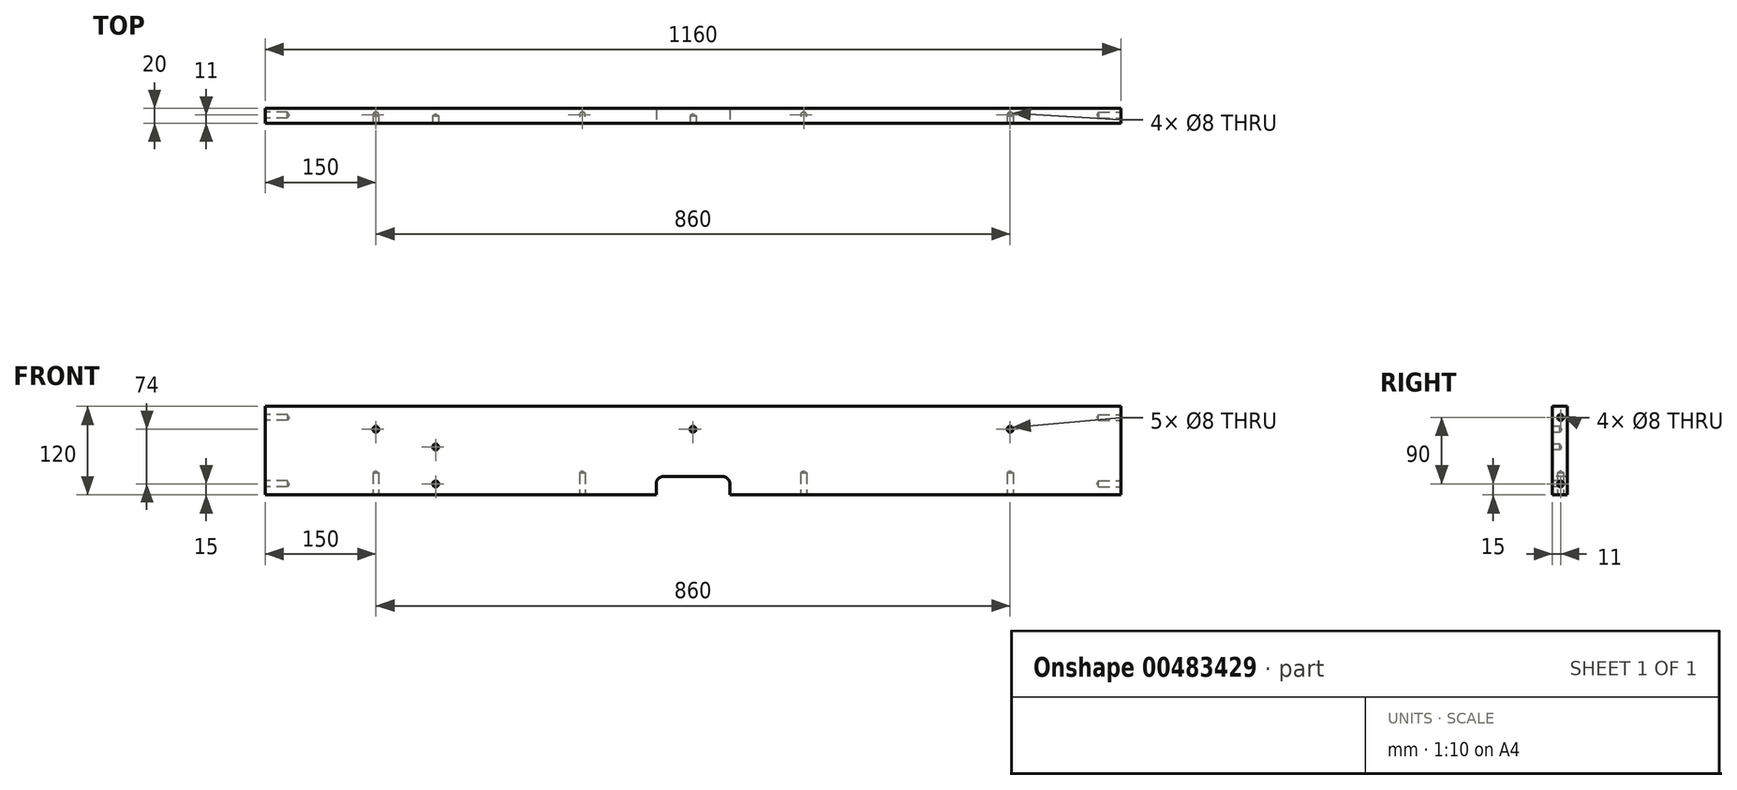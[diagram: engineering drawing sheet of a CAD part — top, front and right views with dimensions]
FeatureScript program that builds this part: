
annotation { "Feature Type Name" : "Feature", "Feature Type Description" : "" }
export const myFeature = defineFeature(function(context is Context, id is Id, definition is map)
    precondition{}
    {
        {
            var Q0;
            Q0=qCreatedBy(makeId("Front.planeOp"),FACE);
            var sketch = newSketch(context, id + "F0", { "sketchPlane" : qUnion([Q0])});
            skLineSegment(sketch, "E0.bottom", {"start": v(580, -60) * mm, "end": v(-580, -60) * mm});
            skLineSegment(sketch, "E0.top", {"start": v(580, 60) * mm, "end": v(-580, 60) * mm});
            skLineSegment(sketch, "E0.left", {"start": v(580, -60) * mm, "end": v(580, 60) * mm});
            skLineSegment(sketch, "E0.right", {"start": v(-580, -60) * mm, "end": v(-580, 60) * mm});
            skPoint(sketch, "E0.middle", {"position": v(0, 0) * mm});
            skSolve(sketch);
        }
        {
            var Q0;
            Q0=makeQuery(id+"F0.imprint","IMPRINT",FACE,{"disambiguationData":[TD([[makeQuery(id+"F0.imprint","IMPRINT",EDGE,{"derivedFrom":sQuery(id+"F0.wireOp",EDGE,"E0.bottom")}),-1.0]])]});
            var Q1;
            Q1=qSketchRegion(id+"F0",true);
            extrude(context, id + "F1", {"entities" : qUnion([Q0, Q1]), "depth" : 20 * mm});
        }
        {
            var Q0;
            Q0=makeQuery(id+"F1.opExtrude","CAP_FACE",FACE,{"disambiguationData":[OSD([sQuery(id+"F0.wireOp",EDGE,"E0.bottom"),sQuery(id+"F0.wireOp",EDGE,"E0.top"),sQuery(id+"F0.wireOp",EDGE,"E0.left"),sQuery(id+"F0.wireOp",EDGE,"E0.right")])],"isStart":false});
            var sketch = newSketch(context, id + "F2", { "sketchPlane" : qUnion([Q0])});
            skLineSegment(sketch, "E1.bottom", {"start": v(-50, -60) * mm, "end": v(50, -60) * mm});
            skLineSegment(sketch, "E1.top", {"start": v(-40, -35) * mm, "end": v(40, -35) * mm});
            skLineSegment(sketch, "E1.left", {"start": v(-50, -60) * mm, "end": v(-50, -45) * mm});
            skLineSegment(sketch, "E1.right", {"start": v(50, -60) * mm, "end": v(50, -45) * mm});
            skPoint(sketch, "E2.visualSharp", {"position": v(-50, -35) * mm});
            skArc(sketch, "E2.filletArc", {"start": v(-40, -35) * mm, "mid": v(-47.07, -37.93) * mm, "end": v(-50, -45) * mm});
            skPoint(sketch, "E3.visualSharp", {"position": v(50, -35) * mm});
            skArc(sketch, "E3.filletArc", {"start": v(50, -45) * mm, "mid": v(47.07, -37.93) * mm, "end": v(40, -35) * mm});
            skSolve(sketch);
        }
        {
            var Q0;
            Q0=qSketchRegion(id+"F2",true);
            extrude(context, id + "F3", {"entities" : qUnion([Q0]), "operationType" : NewBodyOperationType.REMOVE, "endBound" : BoundingType.THROUGH_ALL, "oppositeDirection" : true, "depth" : 25 * mm});
        }
        {
            var Q0;
            Q0=makeQuery(id+"F1.opExtrude","SWEPT_FACE",FACE,{"disambiguationData":[OSD([sQuery(id+"F0.wireOp",EDGE,"E0.right")])]});
            var sketch = newSketch(context, id + "F4", { "sketchPlane" : qUnion([Q0])});
            skPoint(sketch, "E4", {"position": v(9, 45) * mm});
            skPoint(sketch, "E5", {"position": v(9, -45) * mm});
            skSolve(sketch);
        }
        {
            var Q0;
            Q0=makeQuery(id+"F1.opExtrude","SWEPT_FACE",FACE,{"disambiguationData":[OSD([sQuery(id+"F0.wireOp",EDGE,"E0.left")])]});
            var sketch = newSketch(context, id + "F5", { "sketchPlane" : qUnion([Q0])});
            skPoint(sketch, "E6", {"position": v(-9, 45) * mm});
            skPoint(sketch, "E7", {"position": v(-9, -45) * mm});
            skSolve(sketch);
        }
        {
            var Q0;
            Q0=makeQuery(id+"F1.opExtrude","CAP_FACE",FACE,{"disambiguationData":[OSD([sQuery(id+"F0.wireOp",EDGE,"E0.bottom"),sQuery(id+"F0.wireOp",EDGE,"E0.top"),sQuery(id+"F0.wireOp",EDGE,"E0.left"),sQuery(id+"F0.wireOp",EDGE,"E0.right")])],"isStart":false});
            var sketch = newSketch(context, id + "F6", { "sketchPlane" : qUnion([Q0])});
            skPoint(sketch, "E8", {"position": v(-430, 29) * mm});
            skPoint(sketch, "E9", {"position": v(0, 29) * mm});
            skPoint(sketch, "E10", {"position": v(430, 29) * mm});
            skPoint(sketch, "E11", {"position": v(-349, -45) * mm});
            skPoint(sketch, "E12", {"position": v(-349, 5) * mm});
            skSolve(sketch);
        }
        {
            var Q0;
            {var subQ1=sQuery(id+"F0.wireOp",EDGE,"E0.left");var subQ3=sQuery(id+"F0.wireOp",EDGE,"E0.bottom");Q0=makeQuery(id+"F3.boolean.opBoolean","SPLIT",FACE,{"disambiguationData":[TD([makeQuery(id+"F1.opExtrude","SWEPT_FACE",FACE,{"disambiguationData":[OSD([subQ1])]})])],"derivedFrom":makeQuery(id+"F1.opExtrude","SWEPT_FACE",FACE,{"disambiguationData":[OSD([subQ3])]})});}
            var sketch = newSketch(context, id + "F7", { "sketchPlane" : qUnion([Q0])});
            skPoint(sketch, "E13", {"position": v(150, 9) * mm});
            skPoint(sketch, "E14", {"position": v(430, 9) * mm});
            skPoint(sketch, "E15", {"position": v(-150, 9) * mm});
            skPoint(sketch, "E16", {"position": v(-430, 9) * mm});
            skSolve(sketch);
        }
        {
            var Q0;
            Q0=sQuery(id+"F4.wireOp",VERTEX,"E4");
            var Q1;
            Q1=sQuery(id+"F4.wireOp",VERTEX,"E5");
            var Q2;
            Q2=sQuery(id+"F5.wireOp",VERTEX,"E6");
            var Q3;
            Q3=sQuery(id+"F5.wireOp",VERTEX,"E7");
            var Q4;
            Q4=sQuery(id+"F7.wireOp",VERTEX,"E16");
            var Q5;
            Q5=sQuery(id+"F7.wireOp",VERTEX,"E15");
            var Q6;
            Q6=sQuery(id+"F7.wireOp",VERTEX,"E13");
            var Q7;
            Q7=sQuery(id+"F7.wireOp",VERTEX,"E14");
            var Q8;
            Q8=makeQuery(id+"F1.opExtrude","SWEPT_BODY",BODY,{"disambiguationData":[OSD([sQuery(id+"F0.wireOp",EDGE,"E0.bottom"),sQuery(id+"F0.wireOp",EDGE,"E0.top"),sQuery(id+"F0.wireOp",EDGE,"E0.left"),sQuery(id+"F0.wireOp",EDGE,"E0.right")])]});
            hole(context, id + "F8", {"style" : HoleStyle.SIMPLE, "endStyle" : HoleEndStyle.BLIND, "standardTappedOrClearance" : lookupTablePath({ "standard" : "ISO", "size" : "8", "type" : "Drilled" }), "standardBlindInLast" : lookupTablePath({ "standard" : "ISO", "size" : "8", "type" : "Drilled" }), "holeDiameter" : 8 * mm, "holeDepth" : 30 * mm, "isTappedThrough" : true, "tappedDepth" : 12 * mm, "tapClearance" : 3, "locations" : qUnion([Q0, Q1, Q2, Q3, Q4, Q5, Q6, Q7]), "scope" : qUnion([Q8])});
        }
        {
            var Q0;
            Q0=sQuery(id+"F6.wireOp",VERTEX,"E10");
            var Q1;
            Q1=sQuery(id+"F6.wireOp",VERTEX,"E9");
            var Q2;
            Q2=sQuery(id+"F6.wireOp",VERTEX,"E8");
            var Q3;
            Q3=sQuery(id+"F6.wireOp",VERTEX,"E11");
            var Q4;
            Q4=sQuery(id+"F6.wireOp",VERTEX,"E12");
            var Q5;
            Q5=makeQuery(id+"F1.opExtrude","SWEPT_BODY",BODY,{"disambiguationData":[OSD([sQuery(id+"F0.wireOp",EDGE,"E0.bottom"),sQuery(id+"F0.wireOp",EDGE,"E0.top"),sQuery(id+"F0.wireOp",EDGE,"E0.left"),sQuery(id+"F0.wireOp",EDGE,"E0.right")])]});
            hole(context, id + "F9", {"style" : HoleStyle.SIMPLE, "endStyle" : HoleEndStyle.BLIND, "standardTappedOrClearance" : lookupTablePath({ "standard" : "ISO", "size" : "8", "type" : "Drilled" }), "standardBlindInLast" : lookupTablePath({ "standard" : "ISO", "size" : "8", "type" : "Drilled" }), "holeDiameter" : 8 * mm, "holeDepth" : 10 * mm, "isTappedThrough" : true, "tappedDepth" : 12 * mm, "tapClearance" : 3, "locations" : qUnion([Q0, Q1, Q2, Q3, Q4]), "scope" : qUnion([Q5])});
        }
    });
